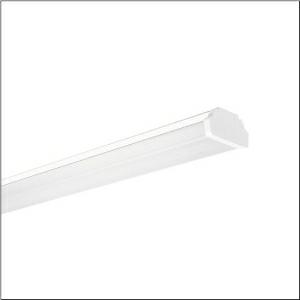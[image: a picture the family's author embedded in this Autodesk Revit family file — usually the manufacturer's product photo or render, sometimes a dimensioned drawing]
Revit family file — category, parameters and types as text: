
# Revit family: dus_r__31_mo_53bd812m1v4085_035f
name_source: partatom
category: Lighting Fixtures
units: mm (PartAtom-declared; Revit-internal decimal feet)

## family parameters
Cut with Voids When Loaded = No
Host = Face
Light Source = No
Part Type = Normal
Room Calculation Point = No
Round Connector Dimension = Use Diameter
Shared = No

## types (1)
- --- (1 x LED, 8950 lm, 59.6 W, 4000K)
    Apparent Load = 60 VA
    CIE Flux Codes = 47 80 95 92 100
    Color Rendering = 80
    Color Temperature = 4000K
    Default Elevation = 1800 mm
    Description = DUS® 31 MOluminaire insert, length: 1.535mm, width: 81mm, height: 90mm, LED rated luminous flux: 8.950lm, light colour: 840, control gear: ON/OFF Multilumen, control gear: ECG Multilumen, with plug, 3-pole, with phase selection, mains connection: 220..240V, AC, 50/60Hz, primary optical cover: cover, of PMMA, light emission: direct distribution, primary light characteristic: symmetric, protection rating (complete): IP20, protection rating (LED compartment): IP50, insulation class (complete): insulation class I (protective earthing), certification: CE, ENEC, VDE, permissible ambient temperature for indoor applications: -35..+30°C, corresponds to IFS (International Featured Standards) requirements for safety and quality in the food industry, reducing of maximum allowable ambient temperature of 5°C with ceiling mounting, packaging unit: 1 piece
    Height = 95 mm
    Lamp = 1 x LED
    Lamp Light Flux = 8950 lm
    Lamp Power = 59.6 W
    Lamp count = 1
    Length = 1535 mm
    Luminous efficacy = 150 lm/W
    Manufacturer = Siteco
    ModVariant = No
    Model = 53BD812M1V4085
    Mounting Place = Ceiling
    Mounting Type = Pendant
    Number of Poles = 1
    OnlyDefault = Yes
    Power Factor = 1
    Product Name = DUS® 31 MO
    Product group = luminaire insert
    ProductGroupID = 902
    Protection Class = Protection class I
    Protection Degree = IP 20
    RLX_Detail_Level = 1
    RlxData = <blob elided: 39709 chars, md5=0b3b590c>
    Socket = socket
    Standby Power = 0 W
    System Light Flux = 8950 lm
    System Power = 60 W
    Type Comments = factory setting: luminous flux: 100 % | (A | C | E) | 129 mA
    Type Image = l_1003451.jpg
    URL = http://relux.com
    VarID = @adj_133703
    Voltage = 0 V
    Weight = 0.00 kg
    Width = 81 mm

## geometry (parser evidence)
native form markers: Blend x4, Sweep x13
no freeform markers — native parametric forms only
